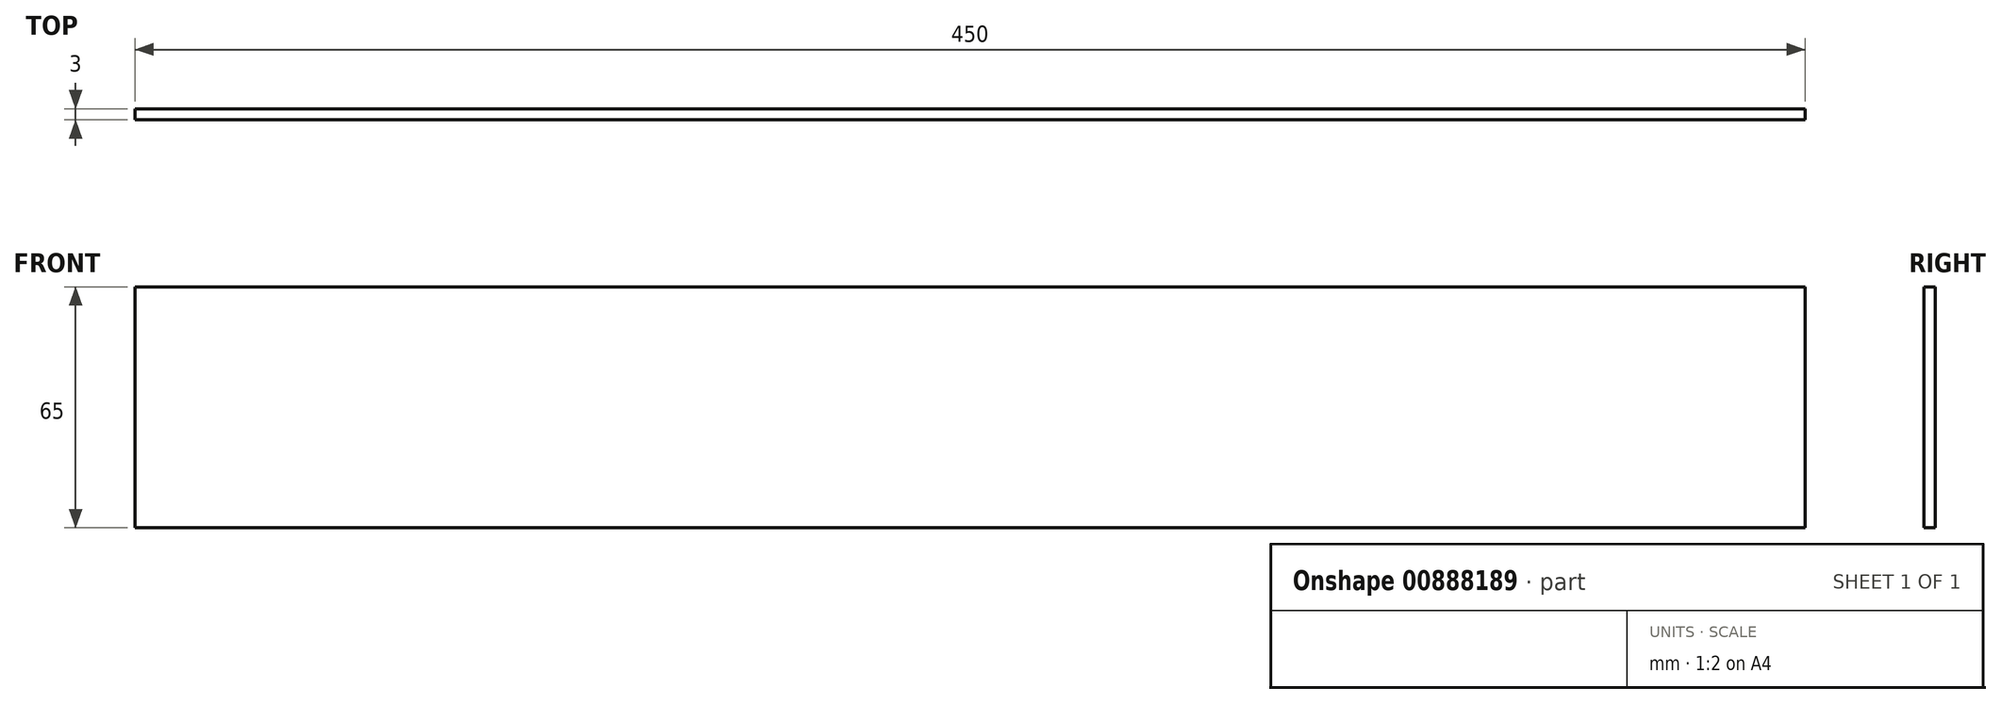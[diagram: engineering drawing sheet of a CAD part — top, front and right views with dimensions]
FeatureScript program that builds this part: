
annotation { "Feature Type Name" : "Feature", "Feature Type Description" : "" }
export const myFeature = defineFeature(function(context is Context, id is Id, definition is map)
    precondition{}
    {
        {
            var Q0;
            Q0=qCreatedBy(makeId("Front.planeOp"),FACE);
            var sketch = newSketch(context, id + "F0", { "sketchPlane" : qUnion([Q0])});
            skLineSegment(sketch, "E0.bottom", {"start": v(-350, 65) * mm, "end": v(100, 65) * mm});
            skLineSegment(sketch, "E0.top", {"start": v(-350, 0) * mm, "end": v(100, 0) * mm});
            skLineSegment(sketch, "E0.left", {"start": v(-350, 65) * mm, "end": v(-350, 0) * mm});
            skLineSegment(sketch, "E0.right", {"start": v(100, 65) * mm, "end": v(100, 0) * mm});
            skSolve(sketch);
        }
        {
            var Q0;
            Q0=makeQuery(id+"F0.imprint","IMPRINT",FACE,{"disambiguationData":[TD([[makeQuery(id+"F0.imprint","IMPRINT",EDGE,{"derivedFrom":sQuery(id+"F0.wireOp",EDGE,"E0.bottom")}),-1.0]])]});
            extrude(context, id + "F1", {"entities" : qUnion([Q0]), "endBound" : BoundingType.SYMMETRIC, "depth" : 3 * mm, "offsetDistance" : 25 * mm});
        }
    });
